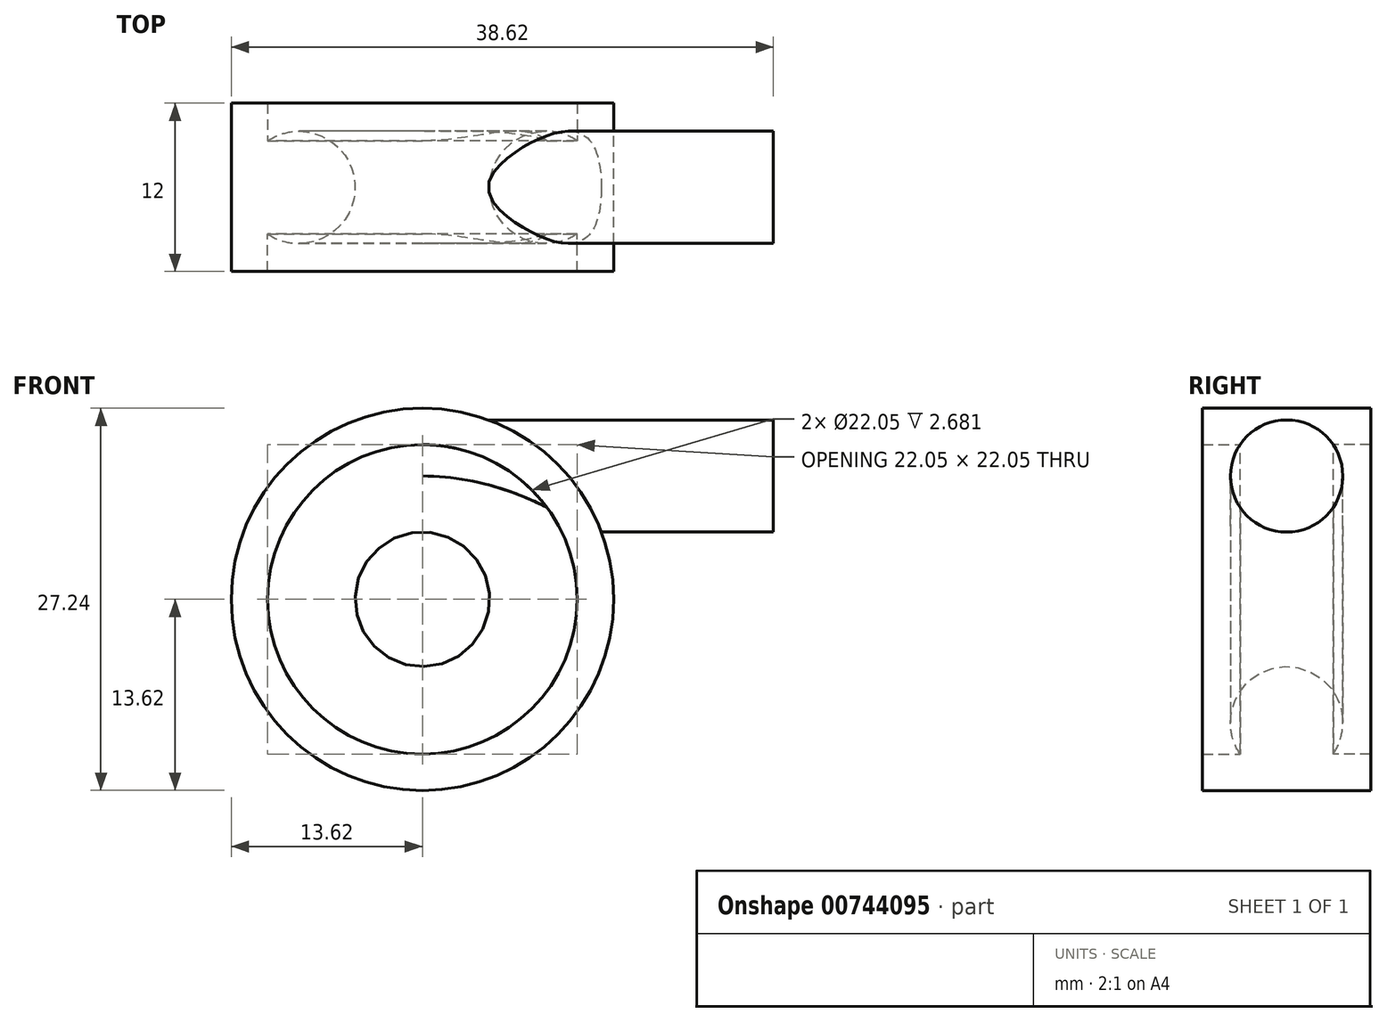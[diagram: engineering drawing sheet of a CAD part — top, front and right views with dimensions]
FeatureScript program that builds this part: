
annotation { "Feature Type Name" : "Feature", "Feature Type Description" : "" }
export const myFeature = defineFeature(function(context is Context, id is Id, definition is map)
    precondition{}
    {
        {
            var Q0;
            Q0=qCreatedBy(makeId("Front.planeOp"),FACE);
            var sketch = newSketch(context, id + "F0", { "sketchPlane" : qUnion([Q0])});
            skCircle(sketch, "E0", {"center": v(0, 0) * mm, "radius": 11.03 * mm});
            skCircle(sketch, "E1.0", {"center": v(0, 0) * mm, "radius": 19.02 * mm});
            skLineSegment(sketch, "E2", {"start": v(0, 19.02) * mm, "end": v(30, 19.02) * mm});
            skCircle(sketch, "E3.0", {"center": v(0, 0) * mm, "radius": 13.62 * mm});
            skSolve(sketch);
        }
        {
            var Q0;
            Q0=qCreatedBy(makeId("Right.planeOp"),FACE);
            var sketch = newSketch(context, id + "F1", { "sketchPlane" : qUnion([Q0])});
            skCircle(sketch, "E4", {"center": v(0, 8.8) * mm, "radius": 4 * mm});
            skSolve(sketch);
        }
        {
            var Q0;
            Q0=makeQuery(id+"F1.imprint","IMPRINT",FACE,{"disambiguationData":[TD([[makeQuery(id+"F1.imprint","IMPRINT",EDGE,{"derivedFrom":sQuery(id+"F1.wireOp",EDGE,"E4")}),1.0]])]});
            var Q1;
            Q1=sQuery(id+"F1.wireOp",EDGE,"E4");
            extrude(context, id + "F2", {"entities" : qUnion([Q0]), "surfaceEntities" : qUnion([Q1]), "depth" : 25 * mm, "offsetDistance" : 25 * mm});
        }
        {
            var Q0;
            Q0=makeQuery(id+"F2.opExtrude","CAP_FACE",FACE,{"disambiguationData":[OSD([sQuery(id+"F1.wireOp",EDGE,"E4")])],"isStart":true});
            var Q1;
            Q1=sQuery(id+"F0.wireOp",EDGE,"E1.0");
            sweep(context, id + "F3", {"operationType" : NewBodyOperationType.ADD, "profiles" : qUnion([Q0]), "path" : qUnion([Q1])});
        }
        {
            var Q0;
            Q0=makeQuery(id+"F0.imprint","IMPRINT",FACE,{"disambiguationData":[TD([[makeQuery(id+"F0.imprint","IMPRINT",EDGE,{"derivedFrom":sQuery(id+"F0.wireOp",EDGE,"E0")}),-1.0]])]});
            extrude(context, id + "F4", {"entities" : qUnion([Q0]), "operationType" : NewBodyOperationType.ADD, "depth" : 6 * mm, "offsetDistance" : 25 * mm});
        }
        {
            var Q0;
            Q0=makeQuery(id+"F2.opExtrude","SWEPT_BODY",BODY,{"disambiguationData":[OSD([sQuery(id+"F1.wireOp",EDGE,"E4")])]});
            var Q1;
            Q1=qCreatedBy(makeId("Front.planeOp"),FACE);
            mirror(context, id + "F5", {"operationType" : NewBodyOperationType.ADD, "entities" : qUnion([Q0]), "mirrorPlane" : qUnion([Q1])});
        }
    });
